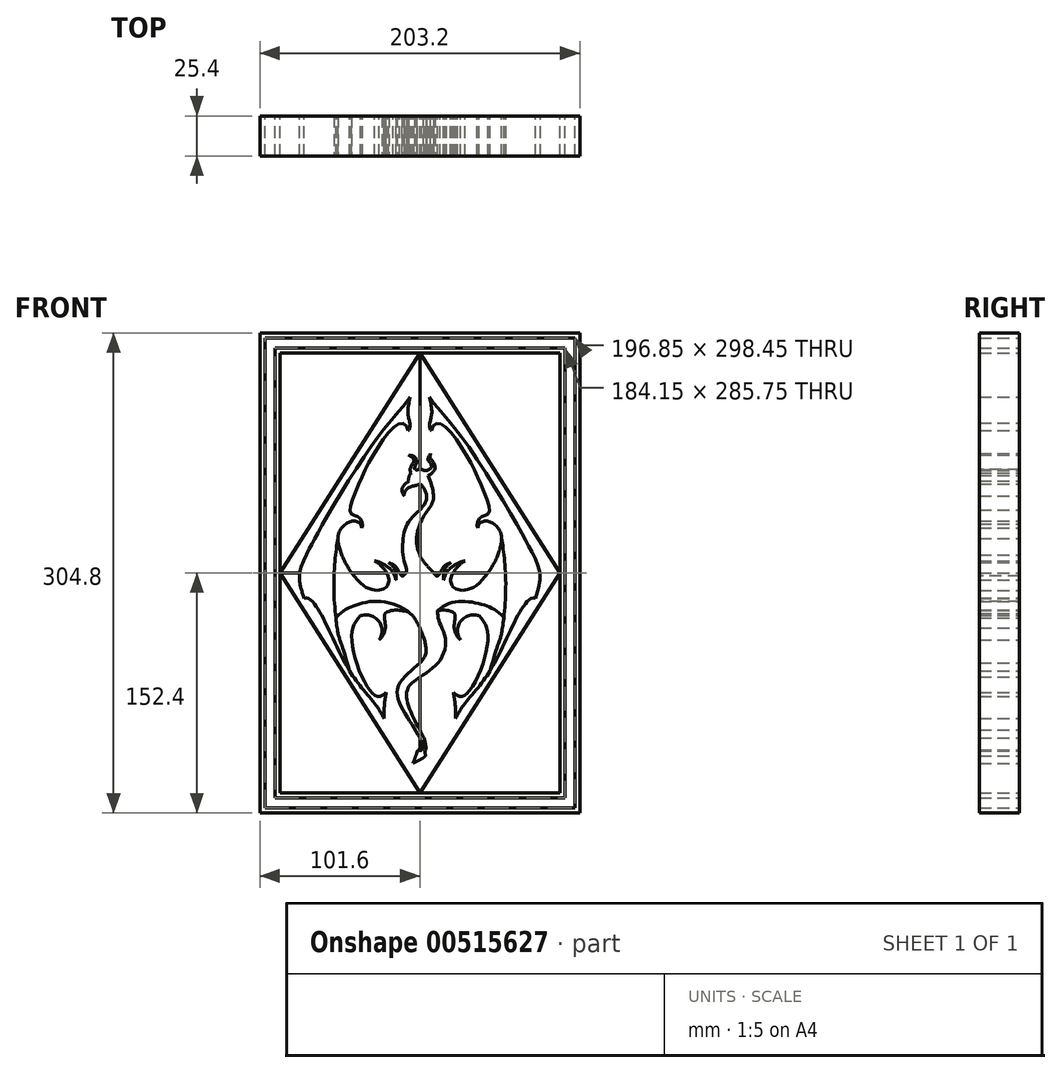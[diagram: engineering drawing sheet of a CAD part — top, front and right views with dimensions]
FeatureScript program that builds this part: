
annotation { "Feature Type Name" : "Feature", "Feature Type Description" : "" }
export const myFeature = defineFeature(function(context is Context, id is Id, definition is map)
    precondition{}
    {
        {
            var Q0;
            Q0=qCreatedBy(makeId("Front.planeOp"),FACE);
            var sketch = newSketch(context, id + "F0", { "sketchPlane" : qUnion([Q0])});
            skLineSegment(sketch, "E0.bottom", {"start": v(101.6, 152.4) * mm, "end": v(-101.6, 152.4) * mm});
            skLineSegment(sketch, "E0.top", {"start": v(101.6, -152.4) * mm, "end": v(-101.6, -152.4) * mm});
            skLineSegment(sketch, "E0.left", {"start": v(101.6, 152.4) * mm, "end": v(101.6, -152.4) * mm});
            skLineSegment(sketch, "E0.right", {"start": v(-101.6, 152.4) * mm, "end": v(-101.6, -152.4) * mm});
            skPoint(sketch, "E0.middle", {"position": v(0, 0) * mm});
            skLineSegment(sketch, "E1.0", {"start": v(98.42, 149.22) * mm, "end": v(-98.43, 149.22) * mm});
            skLineSegment(sketch, "E1.1", {"start": v(98.42, 149.22) * mm, "end": v(98.42, -149.23) * mm});
            skLineSegment(sketch, "E1.2", {"start": v(98.42, -149.23) * mm, "end": v(-98.43, -149.23) * mm});
            skLineSegment(sketch, "E1.3", {"start": v(-98.43, 149.22) * mm, "end": v(-98.43, -149.23) * mm});
            skLineSegment(sketch, "E2.0", {"start": v(92.08, 142.88) * mm, "end": v(-92.08, 142.88) * mm});
            skLineSegment(sketch, "E2.1", {"start": v(92.08, 142.88) * mm, "end": v(92.08, -142.88) * mm});
            skLineSegment(sketch, "E2.2", {"start": v(92.08, -142.88) * mm, "end": v(-92.08, -142.88) * mm});
            skLineSegment(sketch, "E2.3", {"start": v(-92.08, 142.88) * mm, "end": v(-92.08, -142.88) * mm});
            skLineSegment(sketch, "E3.0", {"start": v(88.9, 139.7) * mm, "end": v(-88.9, 139.7) * mm});
            skLineSegment(sketch, "E3.1", {"start": v(88.9, 139.7) * mm, "end": v(88.9, -139.7) * mm});
            skLineSegment(sketch, "E3.2", {"start": v(88.9, -139.7) * mm, "end": v(-88.9, -139.7) * mm});
            skLineSegment(sketch, "E3.3", {"start": v(-88.9, 139.7) * mm, "end": v(-88.9, -139.7) * mm});
            skLineSegment(sketch, "E4", {"start": v(0, 139.7) * mm, "end": v(-88.9, 0) * mm});
            skLineSegment(sketch, "E5", {"start": v(-88.9, 0) * mm, "end": v(0, -139.7) * mm});
            skLineSegment(sketch, "E6", {"start": v(0, -139.7) * mm, "end": v(88.9, 0) * mm});
            skLineSegment(sketch, "E7", {"start": v(88.9, 0) * mm, "end": v(0, 139.7) * mm});
            skLineSegment(sketch, "E8", {"start": v(2.78, 73.03) * mm, "end": v(7.93, 53.64) * mm});
            skLineSegment(sketch, "E9", {"start": v(7.93, 53.64) * mm, "end": v(-10.85, 25.47) * mm});
            skLineSegment(sketch, "E10", {"start": v(-10.85, 25.47) * mm, "end": v(0, 0) * mm});
            skLineSegment(sketch, "E11", {"start": v(0, 0) * mm, "end": v(11.87, -26.98) * mm});
            skLineSegment(sketch, "E12", {"start": v(11.87, -26.98) * mm, "end": v(8.27, -52.2) * mm});
            skLineSegment(sketch, "E13", {"start": v(8.27, -52.2) * mm, "end": v(-11.18, -75.98) * mm});
            skLineSegment(sketch, "E14", {"start": v(-11.18, -75.98) * mm, "end": v(2.77, -107.36) * mm});
            skLineSegment(sketch, "E15", {"start": v(2.78, 73.03) * mm, "end": v(-11.76, 56.07) * mm});
            skLineSegment(sketch, "E16", {"start": v(0, 0) * mm, "end": v(-21.96, -14.5) * mm});
            skLineSegment(sketch, "E17", {"start": v(-21.96, -14.5) * mm, "end": v(-48.7, -10.93) * mm});
            skLineSegment(sketch, "E18", {"start": v(-48.7, -10.93) * mm, "end": v(-67.56, 0) * mm});
            skLineSegment(sketch, "E19", {"start": v(-67.56, 0) * mm, "end": v(-37.58, 62.7) * mm});
            skLineSegment(sketch, "E20", {"start": v(-37.58, 62.7) * mm, "end": v(-9.84, 105.2) * mm});
            skLineSegment(sketch, "E21", {"start": v(-9.84, 105.2) * mm, "end": v(-6.95, 94.04) * mm});
            skLineSegment(sketch, "E22", {"start": v(-67.56, 0) * mm, "end": v(-43.7, -56.2) * mm});
            skLineSegment(sketch, "E23", {"start": v(-43.7, -56.2) * mm, "end": v(-26.41, -81.78) * mm});
            skLineSegment(sketch, "E24", {"start": v(-26.41, -81.78) * mm, "end": v(-22.8, -73.86) * mm});
            skLineSegment(sketch, "E25", {"start": v(2.77, -107.36) * mm, "end": v(8.12, -99.36) * mm});
            skLineSegment(sketch, "E26", {"start": v(0, 0) * mm, "end": v(0, 139.7) * mm, "construction": true});
            skLineSegment(sketch, "E27.MirrorCS", {"start": v(0, 0) * mm, "end": v(21.96, -14.5) * mm});
            skLineSegment(sketch, "E28.MirrorCS", {"start": v(21.96, -14.5) * mm, "end": v(48.7, -10.93) * mm});
            skLineSegment(sketch, "E29.MirrorCS", {"start": v(48.7, -10.93) * mm, "end": v(67.56, 0) * mm});
            skLineSegment(sketch, "E30.MirrorCS", {"start": v(67.56, 0) * mm, "end": v(43.7, -56.2) * mm});
            skLineSegment(sketch, "E31.MirrorCS", {"start": v(43.7, -56.2) * mm, "end": v(26.41, -81.78) * mm});
            skLineSegment(sketch, "E32.MirrorCS", {"start": v(26.41, -81.78) * mm, "end": v(22.8, -73.86) * mm});
            skLineSegment(sketch, "E33.MirrorCS", {"start": v(67.56, 0) * mm, "end": v(37.58, 62.7) * mm});
            skLineSegment(sketch, "E34.MirrorCS", {"start": v(37.58, 62.7) * mm, "end": v(9.84, 105.2) * mm});
            skLineSegment(sketch, "E35.MirrorCS", {"start": v(9.84, 105.2) * mm, "end": v(6.95, 94.04) * mm});
            skSolve(sketch);
        }
        {
            var Q0;
            Q0=qCreatedBy(makeId("Front.planeOp"),FACE);
            var sketch = newSketch(context, id + "F1", { "sketchPlane" : qUnion([Q0])});
            skFitSpline(sketch, "E36", {"points": [v(8.9, 0) * mm, v(1.69, 8.34) * mm, v(-2.03, 20.6) * mm, v(2.3, 35.74) * mm, v(8.48, 46.5) * mm, v(5.1, 61.93) * mm], "startDerivative": vector(-40.38, 43.61) * mm, "endDerivative": vector(-32.31, 77.17) * mm});
            skFitSpline(sketch, "E37", {"points": [v(5.1, 61.93) * mm, v(6.9, 62.9) * mm, v(9.45, 65.8) * mm, v(8.5, 70.37) * mm, v(6.4, 73.48) * mm, v(6.97, 75.8) * mm], "startDerivative": vector(13.53, 3.55) * mm, "endDerivative": vector(6.65, 13.95) * mm});
            skFitSpline(sketch, "E38", {"points": [v(2.67, 65) * mm, v(5.6, 65.53) * mm, v(7.26, 67.15) * mm, v(6.68, 69.87) * mm, v(5.27, 71.89) * mm, v(6.97, 75.8) * mm], "startDerivative": vector(14.88, 1.3) * mm, "endDerivative": vector(11.53, 18.02) * mm});
            skFitSpline(sketch, "E39", {"points": [v(2.67, 65) * mm, v(1.33, 65.7) * mm, v(-1.7, 65.39) * mm], "startDerivative": vector(-1.08, 1.13) * mm, "endDerivative": vector(-1.58, -2.54) * mm});
            skFitSpline(sketch, "E40", {"points": [v(-5.3, 63.38) * mm, v(-6.15, 65.91) * mm, v(-5.1, 68.38) * mm, v(-3.82, 71.06) * mm, v(-4.28, 72.9) * mm, v(-7.18, 74.83) * mm], "startDerivative": vector(-12.95, 10.73) * mm, "endDerivative": vector(-25.98, 12.27) * mm});
            skFitSpline(sketch, "E41", {"points": [v(0.31, 56.47) * mm, v(4.11, 46.37) * mm, v(-5.5, 34.74) * mm, v(-10.33, 23.76) * mm, v(-10.17, 8.58) * mm, v(-8.9, 0) * mm], "startDerivative": vector(39.98, -27.45) * mm, "endDerivative": vector(-19.55, -30.24) * mm});
            skFitSpline(sketch, "E42", {"points": [v(-8.9, 0) * mm, v(-10.89, -1.95) * mm, v(-12.83, 0) * mm, v(-14.9, 3.58) * mm, v(-17.78, 5.85) * mm, v(-19.75, 6.6) * mm], "startDerivative": vector(-9.54, -14.95) * mm, "endDerivative": vector(-11.11, 3.58) * mm});
            skFitSpline(sketch, "E43", {"points": [v(-19.75, 6.6) * mm, v(-17.74, 5.01) * mm, v(-16.11, 2.7) * mm, v(-15.04, -1.41) * mm, v(-15.22, -4.34) * mm], "startDerivative": vector(10.6, -7.66) * mm, "endDerivative": vector(-3.32, -8.06) * mm});
            skFitSpline(sketch, "E44", {"points": [v(-15.22, -4.34) * mm, v(-15.79, -2.3) * mm, v(-17.55, 1.04) * mm, v(-21, 4.37) * mm, v(-28.67, 7.62) * mm], "startDerivative": vector(-1.67, 13.2) * mm, "endDerivative": vector(-21.37, 2.56) * mm});
            skFitSpline(sketch, "E45", {"points": [v(-28.67, 7.62) * mm, v(-25.66, 5.65) * mm, v(-23.07, 3) * mm, v(-20.15, -1.85) * mm, v(-19.93, -6.56) * mm, v(-23.44, -10.26) * mm, v(-36.2, -7.59) * mm, v(-52.01, 21.94) * mm, v(-46.79, 31.32) * mm, v(-41.18, 32.99) * mm, v(-36.9, 28.65) * mm], "startDerivative": vector(61.59, -36.8) * mm, "endDerivative": vector(0, -88.5) * mm});
            skFitSpline(sketch, "E46", {"points": [v(-36.9, 28.65) * mm, v(-36.3, 30.8) * mm, v(-37.86, 34.44) * mm, v(-40.38, 36.31) * mm, v(-43.27, 37.33) * mm, v(-44.29, 41.19) * mm, v(-38.85, 56.32) * mm, v(-30.98, 72.41) * mm, v(-17.61, 91.57) * mm, v(-10.66, 95.01) * mm, v(-7.36, 90.45) * mm], "startDerivative": vector(18.83, 38.8) * mm, "endDerivative": vector(7.96, -64.74) * mm});
            skFitSpline(sketch, "E47", {"points": [v(-7.36, 90.45) * mm, v(-6.23, 92.65) * mm, v(-6.75, 97.2) * mm, v(-7.63, 101.8) * mm, v(-6.29, 111.63) * mm], "startDerivative": vector(10.72, 12.5) * mm, "endDerivative": vector(5.1, 31.48) * mm});
            skFitSpline(sketch, "E48", {"points": [v(-6.29, 111.63) * mm, v(-14.28, 101.55) * mm, v(-32.87, 77.6) * mm, v(-63.36, 27.95) * mm, v(-70.18, 15.38) * mm, v(-75.94, 1.75) * mm, v(-73.4, -16.02) * mm], "startDerivative": vector(-48.69, -84.13) * mm, "endDerivative": vector(63.25, -176.2) * mm});
            skFitSpline(sketch, "E49", {"points": [v(-73.4, -16.02) * mm, v(-68.24, -18.19) * mm, v(-61.24, -28.85) * mm, v(-51.05, -50.12) * mm, v(-39.97, -68.97) * mm, v(-27.23, -84.64) * mm, v(-22.77, -92.41) * mm], "startDerivative": vector(51.52, 22.65) * mm, "endDerivative": vector(27.37, -56.47) * mm});
            skFitSpline(sketch, "E50", {"points": [v(-22.77, -92.41) * mm, v(-22.6, -85.73) * mm, v(-22.07, -80.07) * mm, v(-21.5, -75.93) * mm], "startDerivative": vector(2.46, 25.1) * mm, "endDerivative": vector(0.2, 13.84) * mm});
            skFitSpline(sketch, "E51", {"points": [v(-21.5, -75.93) * mm, v(-25.18, -78.2) * mm, v(-29.6, -76.94) * mm, v(-40.55, -56.2) * mm, v(-42.69, -35.41) * mm, v(-37.55, -27.06) * mm], "startDerivative": vector(-30.8, -27.64) * mm, "endDerivative": vector(37.16, 42.77) * mm});
            skFitSpline(sketch, "E52", {"points": [v(-37.55, -27.06) * mm, v(-30.57, -27.24) * mm, v(-24.67, -33) * mm, v(-25.73, -42.4) * mm], "startDerivative": vector(22.99, 5.57) * mm, "endDerivative": vector(-16.86, -22.13) * mm});
            skFitSpline(sketch, "E53", {"points": [v(-25.73, -42.4) * mm, v(-22.76, -38.55) * mm, v(-21.87, -33.7) * mm, v(-22.44, -28.61) * mm, v(-21.93, -25.68) * mm, v(-17.41, -23.71) * mm, v(-11.32, -23.9) * mm], "startDerivative": vector(20.18, 21.44) * mm, "endDerivative": vector(36.3, -4.89) * mm});
            skFitSpline(sketch, "E54.MirrorCS", {"points": [v(8.9, 0) * mm, v(10.89, -1.95) * mm, v(12.83, 0) * mm, v(14.9, 3.58) * mm, v(17.78, 5.85) * mm, v(19.75, 6.6) * mm], "startDerivative": vector(9.54, -14.95) * mm, "endDerivative": vector(11.11, 3.58) * mm});
            skFitSpline(sketch, "E55.MirrorCS", {"points": [v(19.75, 6.6) * mm, v(17.74, 5.01) * mm, v(16.11, 2.7) * mm, v(15.04, -1.41) * mm, v(15.22, -4.34) * mm], "startDerivative": vector(-10.6, -7.66) * mm, "endDerivative": vector(3.32, -8.06) * mm});
            skFitSpline(sketch, "E56.MirrorCS", {"points": [v(15.22, -4.34) * mm, v(15.79, -2.3) * mm, v(17.55, 1.04) * mm, v(21, 4.37) * mm, v(28.67, 7.62) * mm], "startDerivative": vector(1.67, 13.2) * mm, "endDerivative": vector(21.37, 2.56) * mm});
            skFitSpline(sketch, "E57", {"points": [v(-11.32, -23.9) * mm, v(-6.06, -25.66) * mm, v(1.01, -37.2) * mm, v(3.9, -47.41) * mm, v(1.93, -55.1) * mm, v(-13.87, -72.3) * mm, v(-6.23, -94.21) * mm, v(2.1, -110.37) * mm, v(0.97, -112.63) * mm], "startDerivative": vector(62.88, -6.9) * mm, "endDerivative": vector(-43, -34.49) * mm});
            skFitSpline(sketch, "E58", {"points": [v(11.32, -23.9) * mm, v(12.22, -30.47) * mm, v(16.16, -41.15) * mm, v(12.68, -55.68) * mm, v(0, -66.13) * mm, v(-8.37, -76.43) * mm, v(-0.73, -98.4) * mm, v(2.76, -105.29) * mm, v(3.9, -110.55) * mm, v(3.16, -113.07) * mm], "startDerivative": vector(2.18, -72.8) * mm, "endDerivative": vector(-36.64, -38.6) * mm});
            skFitSpline(sketch, "E59", {"points": [v(3.16, -113.07) * mm, v(3.47, -115.01) * mm, v(3.75, -116.14) * mm], "startDerivative": vector(-0.1, -4.03) * mm, "endDerivative": vector(0.99, -4.67) * mm});
            skFitSpline(sketch, "E60", {"points": [v(3.75, -116.14) * mm, v(2.3, -117.27) * mm, v(1.02, -118.13) * mm, v(0, -118.7) * mm, v(-1.15, -119.25) * mm, v(-2.58, -119.96) * mm, v(-4.4, -120.86) * mm], "startDerivative": vector(-13.57, -10.18) * mm, "endDerivative": vector(-16.34, -7.01) * mm});
            skFitSpline(sketch, "E61", {"points": [v(-4.4, -120.86) * mm, v(-3.32, -118.33) * mm, v(-2.95, -117.2) * mm, v(-2.28, -115.34) * mm, v(-1.36, -112.59) * mm], "startDerivative": vector(9.35, 18.88) * mm, "endDerivative": vector(4.2, 14.27) * mm});
            skFitSpline(sketch, "E62", {"points": [v(-5.3, 63.38) * mm, v(-6.82, 61.48) * mm, v(-6.96, 58.36) * mm], "startDerivative": vector(-5.03, -1.17) * mm, "endDerivative": vector(0.64, -5) * mm});
            skFitSpline(sketch, "E63", {"points": [v(-6.96, 58.36) * mm, v(-9.41, 56.51) * mm, v(-11.34, 52.75) * mm, v(-9.72, 49.04) * mm], "startDerivative": vector(-6.6, -6.29) * mm, "endDerivative": vector(7.73, -5.6) * mm});
            skFitSpline(sketch, "E64", {"points": [v(-9.72, 49.04) * mm, v(-8.54, 52.98) * mm, v(-1.3, 56.08) * mm, v(0.31, 56.47) * mm], "startDerivative": vector(-4.65, 5.77) * mm, "endDerivative": vector(7.04, -2.28) * mm});
            skFitSpline(sketch, "E65", {"points": [v(-1.7, 65.39) * mm, v(-3.05, 65.92) * mm, v(-3.05, 67.58) * mm, v(-2.06, 70.13) * mm, v(-2.38, 72.52) * mm, v(-3.9, 74.08) * mm, v(-7.18, 74.83) * mm], "startDerivative": vector(-11.24, 2.18) * mm, "endDerivative": vector(-17.28, 1.06) * mm});
            skLineSegment(sketch, "E66.0", {"start": v(88.9, 139.7) * mm, "end": v(-88.9, 139.7) * mm});
            skLineSegment(sketch, "E67.0.0", {"start": v(-88.9, 0) * mm, "end": v(0, 139.7) * mm});
            skLineSegment(sketch, "E67.0.1", {"start": v(0, 139.7) * mm, "end": v(-88.9, 139.7) * mm});
            skLineSegment(sketch, "E67.0.2", {"start": v(-88.9, 139.7) * mm, "end": v(-88.9, 0) * mm});
            skLineSegment(sketch, "E68.0.0", {"start": v(0, 139.7) * mm, "end": v(88.9, 0) * mm});
            skLineSegment(sketch, "E68.0.1", {"start": v(88.9, 0) * mm, "end": v(88.9, 139.7) * mm});
            skLineSegment(sketch, "E68.0.2", {"start": v(88.9, 139.7) * mm, "end": v(0, 139.7) * mm});
            skLineSegment(sketch, "E69.0.0", {"start": v(98.42, 149.22) * mm, "end": v(-98.43, 149.22) * mm});
            skLineSegment(sketch, "E69.0.1", {"start": v(-98.43, 149.22) * mm, "end": v(-98.43, -149.23) * mm});
            skLineSegment(sketch, "E69.0.2", {"start": v(-98.43, -149.23) * mm, "end": v(98.42, -149.23) * mm});
            skLineSegment(sketch, "E69.0.3", {"start": v(98.42, -149.23) * mm, "end": v(98.42, 149.22) * mm});
            skLineSegment(sketch, "E70.0", {"start": v(101.6, 152.4) * mm, "end": v(-101.6, 152.4) * mm});
            skLineSegment(sketch, "E71.0.0", {"start": v(92.08, 142.88) * mm, "end": v(-92.08, 142.88) * mm});
            skLineSegment(sketch, "E71.0.1", {"start": v(-92.08, 142.88) * mm, "end": v(-92.08, -142.88) * mm});
            skLineSegment(sketch, "E71.0.2", {"start": v(-92.08, -142.88) * mm, "end": v(92.08, -142.88) * mm});
            skLineSegment(sketch, "E71.0.3", {"start": v(92.08, -142.88) * mm, "end": v(92.08, 142.88) * mm});
            skLineSegment(sketch, "E72.0.0", {"start": v(0, -139.7) * mm, "end": v(-88.9, 0) * mm});
            skLineSegment(sketch, "E72.0.1", {"start": v(-88.9, 0) * mm, "end": v(-88.9, -139.7) * mm});
            skLineSegment(sketch, "E72.0.2", {"start": v(-88.9, -139.7) * mm, "end": v(0, -139.7) * mm});
            skLineSegment(sketch, "E73.0.0", {"start": v(0, -139.7) * mm, "end": v(88.9, -139.7) * mm});
            skLineSegment(sketch, "E73.0.1", {"start": v(88.9, -139.7) * mm, "end": v(88.9, 0) * mm});
            skLineSegment(sketch, "E73.0.2", {"start": v(88.9, 0) * mm, "end": v(0, -139.7) * mm});
            skLineSegment(sketch, "E74", {"start": v(0, 65.85) * mm, "end": v(0, 139.7) * mm});
            skLineSegment(sketch, "E75.trimOffspring", {"start": v(0, 40.13) * mm, "end": v(0, 56.52) * mm});
            skLineSegment(sketch, "E76.trimOffspring", {"start": v(0, 11.4) * mm, "end": v(0, 31.03) * mm});
            skLineSegment(sketch, "E77.trimOffspring", {"start": v(0, -57.17) * mm, "end": v(0, -34.89) * mm});
            skLineSegment(sketch, "E78", {"start": v(-88.9, 0) * mm, "end": v(-76.29, 0) * mm});
            skLineSegment(sketch, "E79.trimOffspring", {"start": v(-43.25, 0) * mm, "end": v(-21, 0) * mm});
            skLineSegment(sketch, "E80.trimOffspring", {"start": v(-16.9, 0) * mm, "end": v(-15.26, 0) * mm});
            skLineSegment(sketch, "E81.trimOffspring", {"start": v(-12.83, 0) * mm, "end": v(-8.9, 0) * mm});
            skLineSegment(sketch, "E82.trimOffspring", {"start": v(8.9, 0) * mm, "end": v(12.83, 0) * mm});
            skLineSegment(sketch, "E83.trimOffspring", {"start": v(20.77, 0) * mm, "end": v(52.54, 0) * mm});
            skLineSegment(sketch, "E84.trimOffspring", {"start": v(15.26, 0) * mm, "end": v(16.9, 0) * mm});
            skLineSegment(sketch, "E85.trimOffspring", {"start": v(76.32, 0) * mm, "end": v(88.9, 0) * mm});
            skLineSegment(sketch, "E86.0", {"start": v(-101.6, 152.4) * mm, "end": v(-101.6, -152.4) * mm});
            skLineSegment(sketch, "E87.0.0", {"start": v(-101.6, -152.4) * mm, "end": v(101.6, -152.4) * mm});
            skLineSegment(sketch, "E87.0.1", {"start": v(101.6, -152.4) * mm, "end": v(101.6, 152.4) * mm});
            skFitSpline(sketch, "E88", {"points": [v(-1.36, -112.59) * mm, v(-0.57, -112.59) * mm, v(0.99, -112.62) * mm], "startDerivative": vector(3.29, 0.82) * mm, "endDerivative": vector(2.87, 0.8) * mm});
            skLineSegment(sketch, "E89", {"start": v(0, -112.04) * mm, "end": v(0, -112.69) * mm});
            skFitSpline(sketch, "E90", {"points": [v(-52.01, 21.94) * mm, v(-54.6, -6.07) * mm, v(-52.03, -37.62) * mm, v(-44.6, -62.11) * mm], "startDerivative": vector(-9.4, -61.75) * mm, "endDerivative": vector(52.36, -183.64) * mm});
            skFitSpline(sketch, "E91", {"points": [v(-53.34, -28.48) * mm, v(-42.4, -20.94) * mm, v(-26.59, -18.02) * mm, v(-6.06, -25.66) * mm], "startDerivative": vector(38, 43.08) * mm, "endDerivative": vector(38.46, -36.93) * mm});
            skFitSpline(sketch, "E92.MirrorCS", {"points": [v(7.36, 90.45) * mm, v(6.23, 92.65) * mm, v(6.75, 97.2) * mm, v(7.63, 101.8) * mm, v(6.29, 111.63) * mm], "startDerivative": vector(-10.72, 12.5) * mm, "endDerivative": vector(-5.1, 31.48) * mm});
            skFitSpline(sketch, "E93.MirrorCS", {"points": [v(6.29, 111.63) * mm, v(14.28, 101.55) * mm, v(32.87, 77.6) * mm, v(63.36, 27.95) * mm, v(70.18, 15.38) * mm, v(75.94, 1.75) * mm, v(73.4, -16.02) * mm], "startDerivative": vector(48.69, -84.13) * mm, "endDerivative": vector(-63.25, -176.2) * mm});
            skFitSpline(sketch, "E94.MirrorCS", {"points": [v(36.9, 28.65) * mm, v(36.3, 30.8) * mm, v(37.86, 34.44) * mm, v(40.38, 36.31) * mm, v(43.27, 37.33) * mm, v(44.29, 41.19) * mm, v(38.85, 56.32) * mm, v(30.98, 72.41) * mm, v(17.61, 91.57) * mm, v(10.66, 95.01) * mm, v(7.36, 90.45) * mm], "startDerivative": vector(-18.83, 38.8) * mm, "endDerivative": vector(-7.96, -64.74) * mm});
            skFitSpline(sketch, "E95.MirrorCS", {"points": [v(28.67, 7.62) * mm, v(25.66, 5.65) * mm, v(23.07, 3) * mm, v(20.15, -1.85) * mm, v(19.93, -6.56) * mm, v(23.44, -10.26) * mm, v(36.2, -7.59) * mm, v(52.01, 21.94) * mm, v(46.79, 31.32) * mm, v(41.18, 32.99) * mm, v(36.9, 28.65) * mm], "startDerivative": vector(-61.59, -36.8) * mm, "endDerivative": vector(0, -88.5) * mm});
            skFitSpline(sketch, "E96.MirrorCS", {"points": [v(52.01, 21.94) * mm, v(54.6, -6.07) * mm, v(52.03, -37.62) * mm, v(44.6, -62.11) * mm], "startDerivative": vector(9.4, -61.75) * mm, "endDerivative": vector(-52.36, -183.64) * mm});
            skFitSpline(sketch, "E97.MirrorCS", {"points": [v(73.4, -16.02) * mm, v(68.24, -18.19) * mm, v(61.24, -28.85) * mm, v(51.05, -50.12) * mm, v(39.97, -68.97) * mm, v(27.23, -84.64) * mm, v(22.77, -92.41) * mm], "startDerivative": vector(-51.52, 22.65) * mm, "endDerivative": vector(-27.37, -56.47) * mm});
            skFitSpline(sketch, "E98.MirrorCS", {"points": [v(37.55, -27.06) * mm, v(30.57, -27.24) * mm, v(24.67, -33) * mm, v(25.73, -42.4) * mm], "startDerivative": vector(-22.99, 5.57) * mm, "endDerivative": vector(16.86, -22.13) * mm});
            skFitSpline(sketch, "E99.MirrorCS", {"points": [v(25.73, -42.4) * mm, v(22.76, -38.55) * mm, v(21.87, -33.7) * mm, v(22.44, -28.61) * mm, v(21.93, -25.68) * mm, v(17.41, -23.71) * mm, v(11.32, -23.9) * mm], "startDerivative": vector(-20.18, 21.44) * mm, "endDerivative": vector(-36.3, -4.89) * mm});
            skFitSpline(sketch, "E100.MirrorCS", {"points": [v(21.5, -75.93) * mm, v(25.18, -78.2) * mm, v(29.6, -76.94) * mm, v(40.55, -56.2) * mm, v(42.69, -35.41) * mm, v(37.55, -27.06) * mm], "startDerivative": vector(30.8, -27.64) * mm, "endDerivative": vector(-37.16, 42.77) * mm});
            skFitSpline(sketch, "E101.MirrorCS", {"points": [v(22.77, -92.41) * mm, v(22.6, -85.73) * mm, v(22.07, -80.07) * mm, v(21.5, -75.93) * mm], "startDerivative": vector(-2.46, 25.1) * mm, "endDerivative": vector(-0.2, 13.84) * mm});
            skFitSpline(sketch, "E102.MirrorCS", {"points": [v(53.34, -28.48) * mm, v(42.4, -20.94) * mm, v(26.59, -18.02) * mm, v(11.32, -23.9) * mm], "startDerivative": vector(-38, 43.08) * mm, "endDerivative": vector(-38.46, -36.93) * mm});
            skLineSegment(sketch, "E103", {"start": v(0, -66.12) * mm, "end": v(0, -99.72) * mm});
            skLineSegment(sketch, "E104.trimOffspring", {"start": v(0, -104.85) * mm, "end": v(0, -112.68) * mm});
            skLineSegment(sketch, "E105.trimOffspring", {"start": v(0, -118.7) * mm, "end": v(0, -139.7) * mm});
            skSolve(sketch);
        }
        {
            var Q0;
            {var subQ42=sQuery(id+"F1.wireOp",EDGE,"E37");Q0=makeQuery(id+"F1.imprint","IMPRINT",FACE,{"disambiguationData":[TD([[makeQuery(id+"F1.imprint","IMPRINT",EDGE,{"derivedFrom":subQ42}),1.0]])]});}
            var Q1;
            Q1=makeQuery(id+"F1.imprint","IMPRINT",FACE,{"disambiguationData":[TD([[makeQuery(id+"F1.imprint","IMPRINT",EDGE,{"derivedFrom":sQuery(id+"F1.wireOp",EDGE,"E73.0.0")}),1.0]])]});
            var Q2;
            Q2=makeQuery(id+"F1.imprint","IMPRINT",FACE,{"disambiguationData":[TD([[makeQuery(id+"F1.imprint","IMPRINT",EDGE,{"derivedFrom":sQuery(id+"F1.wireOp",EDGE,"E68.0.0")}),1.0]])]});
            var Q3;
            Q3=makeQuery(id+"F1.imprint","IMPRINT",FACE,{"disambiguationData":[TD([[makeQuery(id+"F1.imprint","IMPRINT",EDGE,{"derivedFrom":sQuery(id+"F1.wireOp",EDGE,"E67.0.0")}),1.0]])]});
            var Q4;
            Q4=makeQuery(id+"F1.imprint","IMPRINT",FACE,{"disambiguationData":[TD([[makeQuery(id+"F1.imprint","IMPRINT",EDGE,{"derivedFrom":sQuery(id+"F1.wireOp",EDGE,"E72.0.0")}),1.0]])]});
            var Q5;
            Q5=makeQuery(id+"F1.imprint","IMPRINT",FACE,{"disambiguationData":[TD([[makeQuery(id+"F1.imprint","IMPRINT",EDGE,{"derivedFrom":sQuery(id+"F1.wireOp",EDGE,"E69.0.0")}),1.0]])]});
            extrude(context, id + "F2", {"entities" : qUnion([Q0, Q1, Q2, Q3, Q4, Q5]), "depth" : 25.4 * mm, "offsetDistance" : 25.4 * mm});
        }
        {
            var Q0;
            Q0=makeQuery(id+"F1.imprint","IMPRINT",FACE,{"disambiguationData":[TD([[makeQuery(id+"F1.imprint","IMPRINT",EDGE,{"derivedFrom":sQuery(id+"F1.wireOp",EDGE,"E40")}),1.0]])]});
            var Q1;
            {var subQ6=sQuery(id+"F1.wireOp",EDGE,"4451d31d-0079-4f69-9e48-516485929d5c0.MirrorCS");Q1=makeQuery(id+"F1.imprint","IMPRINT",FACE,{"disambiguationData":[TD([[makeQuery(id+"F1.imprint","IMPRINT",EDGE,{"derivedFrom":subQ6}),1.0]])]});}
            var Q2;
            Q2=makeQuery(id+"F1.imprint","IMPRINT",FACE,{"disambiguationData":[TD([[makeQuery(id+"F1.imprint","IMPRINT",EDGE,{"derivedFrom":sQuery(id+"F1.wireOp",EDGE,"E67.0.1")}),-1.0]])]});
            var Q3;
            Q3=makeQuery(id+"F1.imprint","IMPRINT",FACE,{"disambiguationData":[TD([[makeQuery(id+"F1.imprint","IMPRINT",EDGE,{"derivedFrom":sQuery(id+"F1.wireOp",EDGE,"E69.0.0")}),-1.0]])]});
            var Q4;
            {var subQ0=sQuery(id+"F1.wireOp",EDGE,"E83.trimOffspring");Q4=makeQuery(id+"F1.imprint","IMPRINT",FACE,{"disambiguationData":[TD([[makeQuery(id+"F1.imprint","IMPRINT",EDGE,{"derivedFrom":subQ0}),-1.0]])]});}
            var Q5;
            {var subQ3=sQuery(id+"F1.wireOp",EDGE,"E84.trimOffspring");Q5=makeQuery(id+"F1.imprint","IMPRINT",FACE,{"disambiguationData":[TD([[makeQuery(id+"F1.imprint","IMPRINT",EDGE,{"derivedFrom":subQ3}),-1.0]])]});}
            var Q6;
            {var subQ0=sQuery(id+"F1.wireOp",EDGE,"E82.trimOffspring");Q6=makeQuery(id+"F1.imprint","IMPRINT",FACE,{"disambiguationData":[TD([[makeQuery(id+"F1.imprint","IMPRINT",EDGE,{"derivedFrom":subQ0}),-1.0]])]});}
            var Q7;
            {var subQ0=sQuery(id+"F1.wireOp",EDGE,"GVLGkoG3-UP3O-44lH-M6Vz-eQib84nsQOlQ");Q7=makeQuery(id+"F1.imprint","IMPRINT",FACE,{"disambiguationData":[TD([[makeQuery(id+"F1.imprint","IMPRINT",EDGE,{"derivedFrom":subQ0}),-1.0]])]});}
            var Q8;
            {var subQ0=sQuery(id+"F1.wireOp",EDGE,"E77.trimOffspring");Q8=makeQuery(id+"F1.imprint","IMPRINT",FACE,{"disambiguationData":[TD([[makeQuery(id+"F1.imprint","IMPRINT",EDGE,{"derivedFrom":subQ0}),-1.0]])]});}
            var Q9;
            {var subQ0=sQuery(id+"F1.wireOp",EDGE,"E76.trimOffspring");Q9=makeQuery(id+"F1.imprint","IMPRINT",FACE,{"disambiguationData":[TD([[makeQuery(id+"F1.imprint","IMPRINT",EDGE,{"derivedFrom":subQ0}),1.0]])]});}
            var Q10;
            {var subQ0=sQuery(id+"F1.wireOp",EDGE,"E50");Q10=makeQuery(id+"F1.imprint","IMPRINT",FACE,{"disambiguationData":[TD([[makeQuery(id+"F1.imprint","IMPRINT",EDGE,{"derivedFrom":subQ0}),1.0]])]});}
            var Q11;
            Q11=makeQuery(id+"F1.imprint","IMPRINT",FACE,{"disambiguationData":[TD([[makeQuery(id+"F1.imprint","IMPRINT",EDGE,{"derivedFrom":sQuery(id+"F1.wireOp",EDGE,"E92.MirrorCS")}),-1.0]])]});
            extrude(context, id + "F3", {"entities" : qUnion([Q0, Q1, Q2, Q3, Q4, Q5, Q6, Q7, Q8, Q9, Q10, Q11]), "depth" : 25.4 * mm, "offsetDistance" : 25.4 * mm});
        }
        {
            var Q0;
            {var subQ15=sQuery(id+"F1.wireOp",EDGE,"E37");Q0=makeQuery(id+"F1.imprint","IMPRINT",FACE,{"disambiguationData":[TD([[makeQuery(id+"F1.imprint","IMPRINT",EDGE,{"derivedFrom":subQ15}),-1.0]])]});}
            var Q1;
            {var subQ6=sQuery(id+"F1.wireOp",EDGE,"E49");Q1=makeQuery(id+"F1.imprint","IMPRINT",FACE,{"disambiguationData":[TD([[makeQuery(id+"F1.imprint","IMPRINT",EDGE,{"derivedFrom":subQ6}),-1.0]])]});}
            var Q2;
            {var subQ0=sQuery(id+"F1.wireOp",EDGE,"7728c9e4-0d7e-4d33-8bca-7447fd1dce3c.trimOffspring");Q2=makeQuery(id+"F1.imprint","IMPRINT",FACE,{"disambiguationData":[TD([[makeQuery(id+"F1.imprint","IMPRINT",EDGE,{"derivedFrom":subQ0}),1.0]])]});}
            var Q3;
            {var subQ0=sQuery(id+"F1.wireOp",EDGE,"E79.trimOffspring");Q3=makeQuery(id+"F1.imprint","IMPRINT",FACE,{"disambiguationData":[TD([[makeQuery(id+"F1.imprint","IMPRINT",EDGE,{"derivedFrom":subQ0}),-1.0]])]});}
            var Q4;
            {var subQ0=sQuery(id+"F1.wireOp",EDGE,"E81.trimOffspring");Q4=makeQuery(id+"F1.imprint","IMPRINT",FACE,{"disambiguationData":[TD([[makeQuery(id+"F1.imprint","IMPRINT",EDGE,{"derivedFrom":subQ0}),-1.0]])]});}
            var Q5;
            {var subQ3=sQuery(id+"F1.wireOp",EDGE,"E80.trimOffspring");Q5=makeQuery(id+"F1.imprint","IMPRINT",FACE,{"disambiguationData":[TD([[makeQuery(id+"F1.imprint","IMPRINT",EDGE,{"derivedFrom":subQ3}),-1.0]])]});}
            var Q6;
            {var subQ3=sQuery(id+"F1.wireOp",EDGE,"E75.trimOffspring");Q6=makeQuery(id+"F1.imprint","IMPRINT",FACE,{"disambiguationData":[TD([[makeQuery(id+"F1.imprint","IMPRINT",EDGE,{"derivedFrom":subQ3}),-1.0]])]});}
            extrude(context, id + "F4", {"entities" : qUnion([Q0, Q1, Q2, Q3, Q4, Q5, Q6]), "depth" : 25.4 * mm, "offsetDistance" : 25.4 * mm});
        }
        {
            var Q0;
            {var subQ3=sQuery(id+"F1.wireOp",EDGE,"E46");Q0=makeQuery(id+"F1.imprint","IMPRINT",FACE,{"disambiguationData":[TD([[makeQuery(id+"F1.imprint","IMPRINT",EDGE,{"derivedFrom":subQ3}),1.0]])]});}
            var Q1;
            Q1=makeQuery(id+"F1.imprint","IMPRINT",FACE,{"disambiguationData":[TD([[makeQuery(id+"F1.imprint","IMPRINT",EDGE,{"derivedFrom":sQuery(id+"F1.wireOp",EDGE,"E98.MirrorCS")}),-1.0]])]});
            var Q2;
            {var subQ0=sQuery(id+"F1.wireOp",EDGE,"E103");Q2=makeQuery(id+"F1.imprint","IMPRINT",FACE,{"disambiguationData":[TD([[makeQuery(id+"F1.imprint","IMPRINT",EDGE,{"derivedFrom":subQ0}),-1.0]])]});}
            var Q3;
            {var subQ3=sQuery(id+"F1.wireOp",EDGE,"E104.trimOffspring");Q3=makeQuery(id+"F1.imprint","IMPRINT",FACE,{"disambiguationData":[TD([[makeQuery(id+"F1.imprint","IMPRINT",EDGE,{"derivedFrom":subQ3}),1.0]])]});}
            extrude(context, id + "F5", {"entities" : qUnion([Q0, Q1, Q2, Q3]), "depth" : 25.4 * mm, "offsetDistance" : 25.4 * mm});
        }
    });
